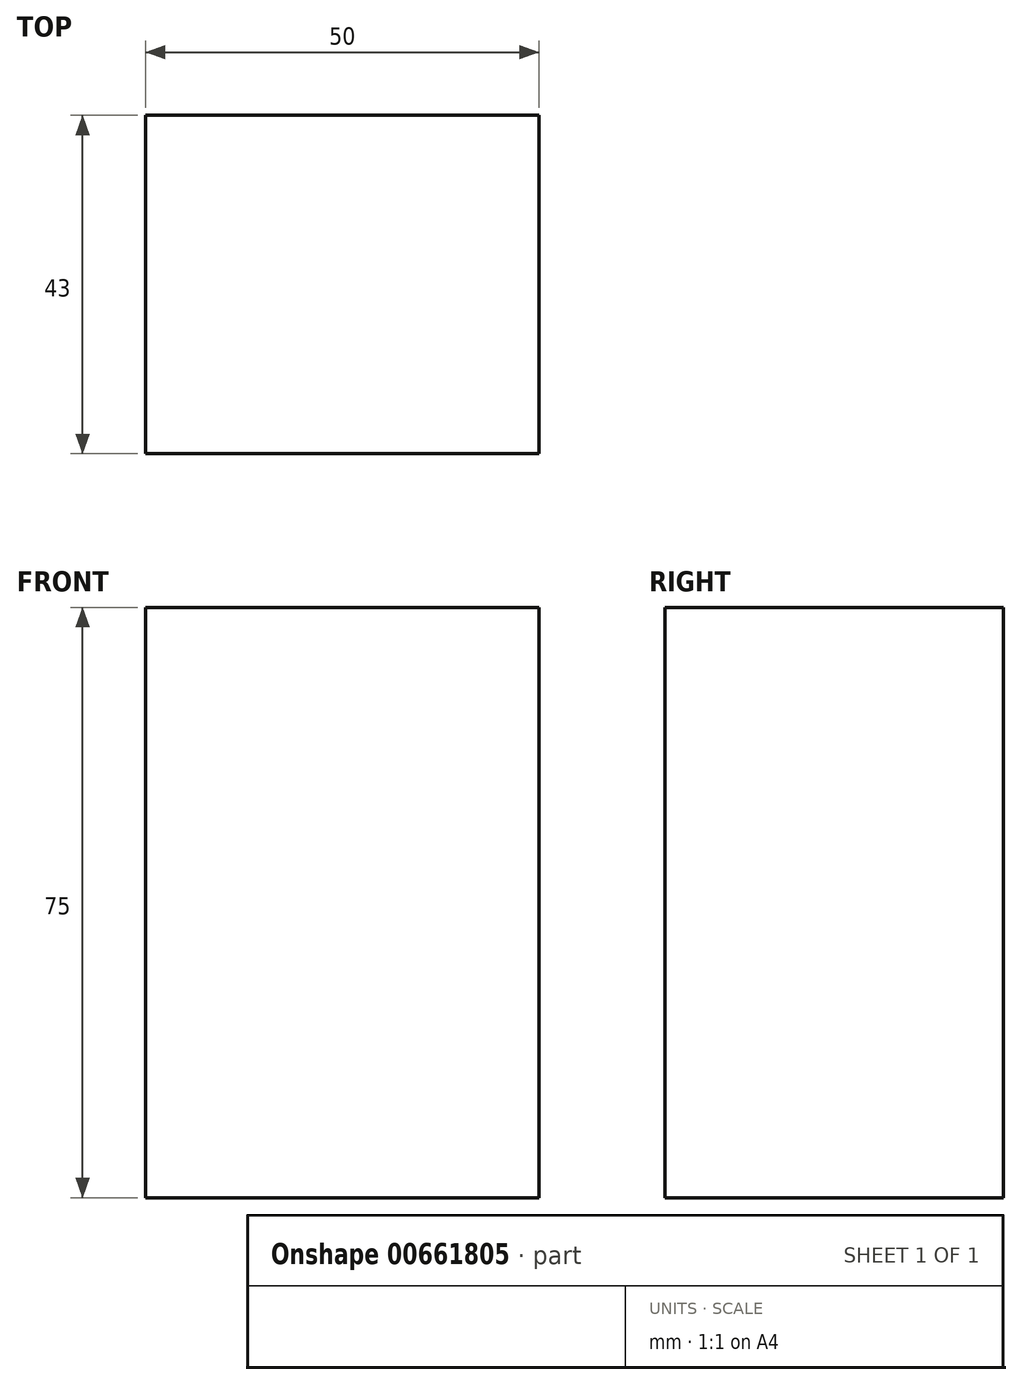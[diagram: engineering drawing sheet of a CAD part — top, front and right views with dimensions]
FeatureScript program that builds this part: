
annotation { "Feature Type Name" : "Feature", "Feature Type Description" : "" }
export const myFeature = defineFeature(function(context is Context, id is Id, definition is map)
    precondition{}
    {
        {
            var Q0;
            Q0=qCreatedBy(makeId("Top.planeOp"),FACE);
            var sketch = newSketch(context, id + "F0", { "sketchPlane" : qUnion([Q0])});
            skLineSegment(sketch, "E0.bottom", {"start": v(-41.25, 23.95) * mm, "end": v(8.75, 23.95) * mm});
            skLineSegment(sketch, "E0.top", {"start": v(-41.25, -19.05) * mm, "end": v(8.75, -19.05) * mm});
            skLineSegment(sketch, "E0.left", {"start": v(-41.25, 23.95) * mm, "end": v(-41.25, -19.05) * mm});
            skLineSegment(sketch, "E0.right", {"start": v(8.75, 23.95) * mm, "end": v(8.75, -19.05) * mm});
            skSolve(sketch);
        }
        {
            var Q0;
            Q0 = qSketchRegion(id + "F0", true);
            extrude(context, id + "F1", {"entities" : qUnion([Q0]), "depth" : 75 * mm, "offsetDistance" : 25 * mm});
        }
    });
